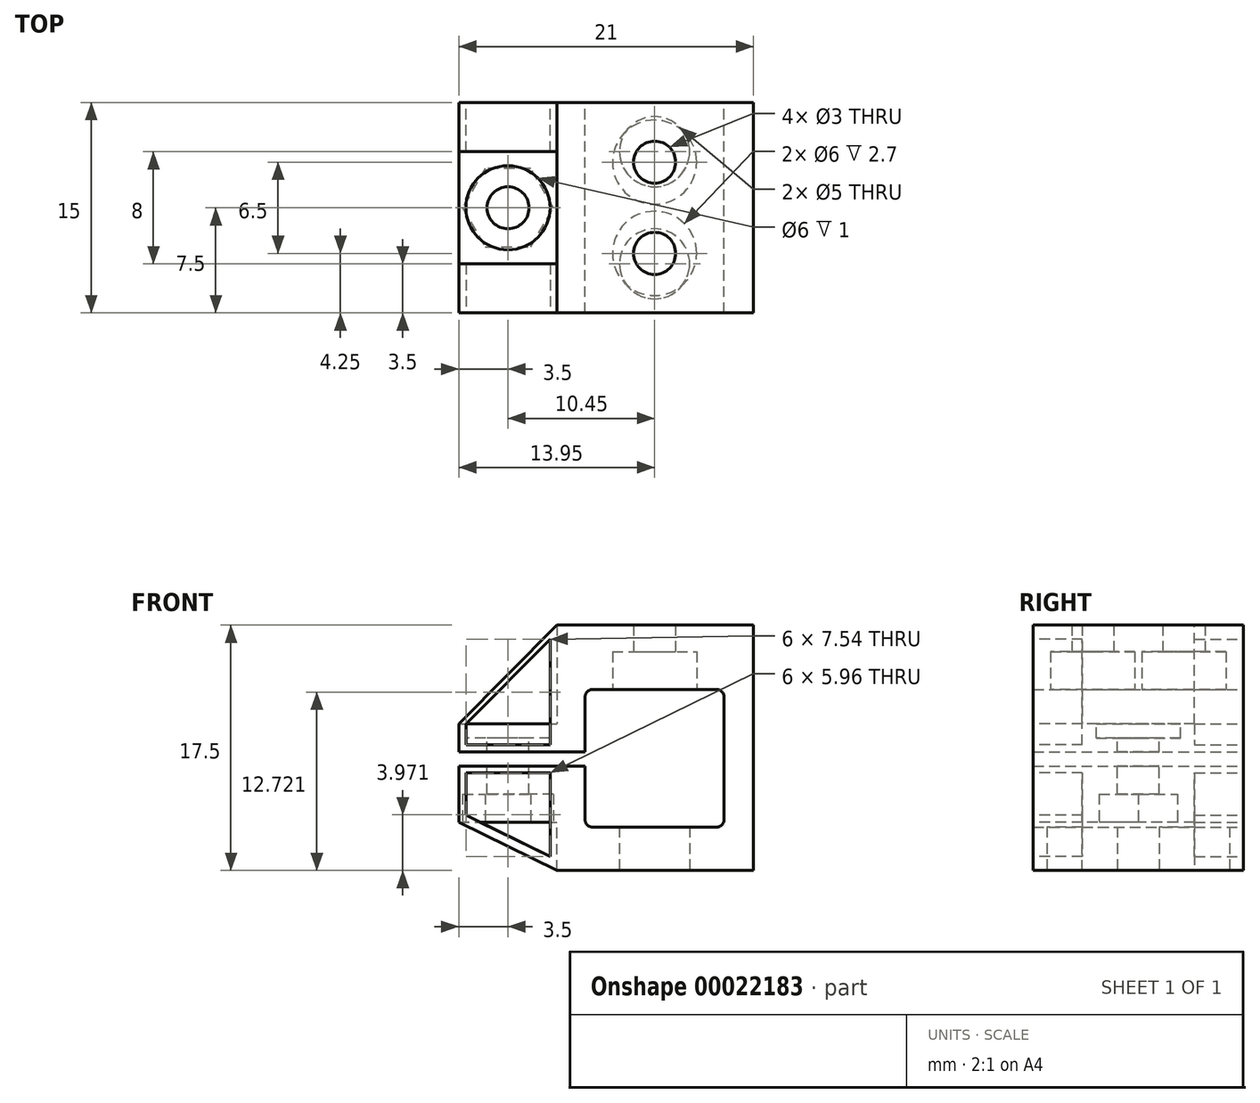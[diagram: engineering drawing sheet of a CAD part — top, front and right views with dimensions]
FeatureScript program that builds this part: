
annotation { "Feature Type Name" : "Feature", "Feature Type Description" : "" }
export const myFeature = defineFeature(function(context is Context, id is Id, definition is map)
    precondition{}
    {
        {
            var Q0;
            Q0=qCreatedBy(makeId("Front.planeOp"),FACE);
            var sketch = newSketch(context, id + "F0", { "sketchPlane" : qUnion([Q0])});
            skLineSegment(sketch, "E0.rect.bottom", {"start": v(-4.45, 4.9) * mm, "end": v(4.45, 4.9) * mm});
            skLineSegment(sketch, "E0.rect.top", {"start": v(-4.45, -4.9) * mm, "end": v(4.45, -4.9) * mm});
            skLineSegment(sketch, "E0.rect.left", {"start": v(-4.95, 4.4) * mm, "end": v(-4.95, -4.4) * mm});
            skLineSegment(sketch, "E0.rect.right", {"start": v(4.95, 4.4) * mm, "end": v(4.95, -4.4) * mm});
            skPoint(sketch, "E0.rect.middle", {"position": v(0, 0) * mm});
            skPoint(sketch, "E1.visualSharp", {"position": v(-4.95, 4.9) * mm});
            skArc(sketch, "E1.filletArc", {"start": v(-4.45, 4.9) * mm, "mid": v(-4.8, 4.75) * mm, "end": v(-4.95, 4.4) * mm});
            skPoint(sketch, "E2.visualSharp", {"position": v(4.95, 4.9) * mm});
            skArc(sketch, "E2.filletArc", {"start": v(4.95, 4.4) * mm, "mid": v(4.8, 4.75) * mm, "end": v(4.45, 4.9) * mm});
            skPoint(sketch, "E3.visualSharp", {"position": v(4.95, -4.9) * mm});
            skArc(sketch, "E3.filletArc", {"start": v(4.45, -4.9) * mm, "mid": v(4.8, -4.75) * mm, "end": v(4.95, -4.4) * mm});
            skPoint(sketch, "E4.visualSharp", {"position": v(-4.95, -4.9) * mm});
            skArc(sketch, "E4.filletArc", {"start": v(-4.95, -4.4) * mm, "mid": v(-4.8, -4.75) * mm, "end": v(-4.45, -4.9) * mm});
            skLineSegment(sketch, "E5", {"start": v(-4.95, -0.55) * mm, "end": v(-6.95, -0.55) * mm});
            skLineSegment(sketch, "E6", {"start": v(-6.95, -0.55) * mm, "end": v(-6.95, -8) * mm});
            skLineSegment(sketch, "E7", {"start": v(-6.95, -8) * mm, "end": v(7.05, -8) * mm});
            skLineSegment(sketch, "E8", {"start": v(7.05, -8) * mm, "end": v(7.05, 9.5) * mm});
            skLineSegment(sketch, "E9", {"start": v(7.05, 9.5) * mm, "end": v(-6.95, 9.5) * mm});
            skLineSegment(sketch, "E10", {"start": v(-6.95, 9.5) * mm, "end": v(-6.95, 0.45) * mm});
            skLineSegment(sketch, "E11", {"start": v(-6.95, 0.45) * mm, "end": v(-4.95, 0.45) * mm});
            skSolve(sketch);
        }
        {
            var Q0;
            Q0=makeQuery(id+"F0.imprint","IMPRINT",FACE,{"disambiguationData":[TD([[makeQuery(id+"F0.imprint","IMPRINT",EDGE,{"derivedFrom":sQuery(id+"F0.wireOp",EDGE,"E0.rect.bottom")}),1.0]])]});
            extrude(context, id + "F1", {"entities" : qUnion([Q0]), "depth" : 15 * mm});
        }
        {
            var Q0;
            Q0=makeQuery(id+"F1.opExtrude","SWEPT_FACE",FACE,{"disambiguationData":[OSD([sQuery(id+"F0.wireOp",EDGE,"E10")])]});
            var sketch = newSketch(context, id + "F2", { "sketchPlane" : qUnion([Q0])});
            skLineSegment(sketch, "E12.bottom", {"start": v(3.5, 0.45) * mm, "end": v(11.5, 0.45) * mm});
            skLineSegment(sketch, "E12.top", {"start": v(3.5, 2.45) * mm, "end": v(11.5, 2.45) * mm});
            skLineSegment(sketch, "E12.left", {"start": v(3.5, 0.45) * mm, "end": v(3.5, 2.45) * mm});
            skLineSegment(sketch, "E12.right", {"start": v(11.5, 0.45) * mm, "end": v(11.5, 2.45) * mm});
            skLineSegment(sketch, "E13.bottom", {"start": v(3.5, -0.55) * mm, "end": v(11.5, -0.55) * mm});
            skLineSegment(sketch, "E13.top", {"start": v(3.5, -4.55) * mm, "end": v(11.5, -4.55) * mm});
            skLineSegment(sketch, "E13.left", {"start": v(3.5, -0.55) * mm, "end": v(3.5, -4.55) * mm});
            skLineSegment(sketch, "E13.right", {"start": v(11.5, -0.55) * mm, "end": v(11.5, -4.55) * mm});
            skSolve(sketch);
        }
        {
            var Q0;
            Q0 = qSketchRegion(id + "F2", true);
            extrude(context, id + "F3", {"entities" : qUnion([Q0]), "operationType" : NewBodyOperationType.ADD, "depth" : 7 * mm});
        }
        {
            var Q0;
            Q0=makeQuery(id+"F3.opExtrude","SWEPT_FACE",FACE,{"disambiguationData":[OSD([sQuery(id+"F2.wireOp",EDGE,"E12.top")])]});
            var sketch = newSketch(context, id + "F4", { "sketchPlane" : qUnion([Q0])});
            skLineSegment(sketch, "E14", {"start": v(-10.45, -11.5) * mm, "end": v(-10.45, -3.5) * mm, "construction": true});
            skCircle(sketch, "E15", {"center": v(-10.45, -7.5) * mm, "radius": 1.5 * mm});
            skCircle(sketch, "E16", {"center": v(-10.45, -7.5) * mm, "radius": 3 * mm});
            skSolve(sketch);
        }
        {
            var Q0;
            Q0=makeQuery(id+"F4.imprint","IMPRINT",FACE,{"disambiguationData":[TD([[makeQuery(id+"F4.imprint","IMPRINT",EDGE,{"derivedFrom":sQuery(id+"F4.wireOp",EDGE,"E15")}),1.0]])]});
            extrude(context, id + "F5", {"entities" : qUnion([Q0]), "operationType" : NewBodyOperationType.REMOVE, "endBound" : BoundingType.THROUGH_ALL, "oppositeDirection" : true, "depth" : 25 * mm});
        }
        {
            var Q0;
            Q0 = qSketchRegion(id + "F4", true);
            extrude(context, id + "F6", {"entities" : qUnion([Q0]), "operationType" : NewBodyOperationType.REMOVE, "oppositeDirection" : true, "depth" : 1 * mm});
        }
        {
            var Q0;
            Q0=makeQuery(id+"F1.opExtrude","SWEPT_FACE",FACE,{"disambiguationData":[OSD([sQuery(id+"F0.wireOp",EDGE,"E0.rect.bottom")])]});
            var sketch = newSketch(context, id + "F7", { "sketchPlane" : qUnion([Q0])});
            skLineSegment(sketch, "E17", {"start": v(0, 15) * mm, "end": v(0, 0) * mm, "construction": true});
            skCircle(sketch, "E18", {"center": v(0, 10.75) * mm, "radius": 3 * mm});
            skCircle(sketch, "E19", {"center": v(0, 4.25) * mm, "radius": 3 * mm});
            skLineSegment(sketch, "E20", {"start": v(-4.45, 7.5) * mm, "end": v(4.45, 7.5) * mm, "construction": true});
            skCircle(sketch, "E21", {"center": v(0, 10.75) * mm, "radius": 1.5 * mm});
            skCircle(sketch, "E22", {"center": v(0, 4.25) * mm, "radius": 1.5 * mm});
            skSolve(sketch);
        }
        {
            var Q0;
            Q0=makeQuery(id+"F7.imprint","IMPRINT",FACE,{"disambiguationData":[TD([[makeQuery(id+"F7.imprint","IMPRINT",EDGE,{"derivedFrom":sQuery(id+"F7.wireOp",EDGE,"E21")}),1.0]])]});
            var Q1;
            Q1=makeQuery(id+"F7.imprint","IMPRINT",FACE,{"disambiguationData":[TD([[makeQuery(id+"F7.imprint","IMPRINT",EDGE,{"derivedFrom":sQuery(id+"F7.wireOp",EDGE,"E22")}),1.0]])]});
            extrude(context, id + "F8", {"entities" : qUnion([Q0, Q1]), "operationType" : NewBodyOperationType.REMOVE, "endBound" : BoundingType.THROUGH_ALL, "oppositeDirection" : true, "depth" : 25 * mm});
        }
        {
            var Q0;
            Q0 = qSketchRegion(id + "F7", true);
            extrude(context, id + "F9", {"entities" : qUnion([Q0]), "operationType" : NewBodyOperationType.REMOVE, "oppositeDirection" : true, "depth" : 2.7 * mm});
        }
        {
            var Q0;
            Q0=makeQuery(id+"F1.opExtrude","SWEPT_FACE",FACE,{"disambiguationData":[OSD([sQuery(id+"F0.wireOp",EDGE,"E7")])]});
            var sketch = newSketch(context, id + "F10", { "sketchPlane" : qUnion([Q0])});
            skLineSegment(sketch, "E23", {"start": v(0, 0) * mm, "end": v(0, 15) * mm, "construction": true});
            skPoint(sketch, "E24.rect.middle", {"position": v(0, 7.5) * mm});
            skCircle(sketch, "E25", {"center": v(0, 11.5) * mm, "radius": 2.5 * mm});
            skCircle(sketch, "E26", {"center": v(0, 3.5) * mm, "radius": 2.5 * mm});
            skSolve(sketch);
        }
        {
            var Q0;
            Q0 = qSketchRegion(id + "F10", true);
            var Q1;
            Q1=makeQuery(id+"F1.opExtrude","SWEPT_FACE",FACE,{"disambiguationData":[OSD([sQuery(id+"F0.wireOp",EDGE,"E0.rect.top")])]});
            extrude(context, id + "F11", {"entities" : qUnion([Q0]), "operationType" : NewBodyOperationType.REMOVE, "endBound" : BoundingType.UP_TO_SURFACE, "oppositeDirection" : true, "endBoundEntityFace" : qUnion([Q1]), "depth" : 25 * mm});
        }
        {
            var Q0;
            Q0=makeQuery(id+"F3.opExtrude","SWEPT_FACE",FACE,{"disambiguationData":[OSD([sQuery(id+"F2.wireOp",EDGE,"E13.top")])]});
            var sketch = newSketch(context, id + "F12", { "sketchPlane" : qUnion([Q0])});
            skCircle(sketch, "E27.cCircle", {"center": v(-10.45, 7.5) * mm, "radius": 2.8 * mm, "construction": true});
            skLineSegment(sketch, "E27.0", {"start": v(-8.83, 4.7) * mm, "end": v(-12.07, 4.7) * mm});
            skLineSegment(sketch, "E27.1", {"start": v(-12.07, 4.7) * mm, "end": v(-13.68, 7.5) * mm});
            skLineSegment(sketch, "E27.2", {"start": v(-13.68, 7.5) * mm, "end": v(-12.07, 10.3) * mm});
            skLineSegment(sketch, "E27.3", {"start": v(-12.07, 10.3) * mm, "end": v(-8.83, 10.3) * mm});
            skLineSegment(sketch, "E27.4", {"start": v(-8.83, 10.3) * mm, "end": v(-7.22, 7.5) * mm});
            skLineSegment(sketch, "E27.5", {"start": v(-7.22, 7.5) * mm, "end": v(-8.83, 4.7) * mm});
            skPoint(sketch, "E27.0.midPoint", {"position": v(-10.45, 4.7) * mm});
            skSolve(sketch);
        }
        {
            var Q0;
            Q0 = qSketchRegion(id + "F12", true);
            extrude(context, id + "F13", {"entities" : qUnion([Q0]), "operationType" : NewBodyOperationType.REMOVE, "oppositeDirection" : true, "depth" : 2 * mm});
        }
        {
            var Q0;
            Q0=makeQuery(id+"F1.opExtrude","CAP_FACE",FACE,{"disambiguationData":[OSD([sQuery(id+"F0.wireOp",EDGE,"E0.rect.bottom"),sQuery(id+"F0.wireOp",EDGE,"E0.rect.top"),sQuery(id+"F0.wireOp",EDGE,"E0.rect.left"),sQuery(id+"F0.wireOp",EDGE,"E0.rect.right"),sQuery(id+"F0.wireOp",EDGE,"E1.filletArc"),sQuery(id+"F0.wireOp",EDGE,"E2.filletArc"),sQuery(id+"F0.wireOp",EDGE,"E3.filletArc"),sQuery(id+"F0.wireOp",EDGE,"E4.filletArc"),sQuery(id+"F0.wireOp",EDGE,"E5"),sQuery(id+"F0.wireOp",EDGE,"E6"),sQuery(id+"F0.wireOp",EDGE,"E7"),sQuery(id+"F0.wireOp",EDGE,"E8"),sQuery(id+"F0.wireOp",EDGE,"E9"),sQuery(id+"F0.wireOp",EDGE,"E10"),sQuery(id+"F0.wireOp",EDGE,"E11")])],"isStart":true});
            var sketch = newSketch(context, id + "F14", { "sketchPlane" : qUnion([Q0])});
            skLineSegment(sketch, "E28", {"start": v(6.95, 9.5) * mm, "end": v(13.95, 2.45) * mm});
            skLineSegment(sketch, "E29", {"start": v(13.95, 2.45) * mm, "end": v(13.95, 0.45) * mm});
            skLineSegment(sketch, "E30", {"start": v(13.95, 0.45) * mm, "end": v(6.95, 0.45) * mm});
            skLineSegment(sketch, "E31", {"start": v(6.95, 0.45) * mm, "end": v(6.95, 9.5) * mm});
            skLineSegment(sketch, "E32", {"start": v(7.45, 8.5) * mm, "end": v(13.45, 2.45) * mm});
            skLineSegment(sketch, "E33", {"start": v(13.45, 2.45) * mm, "end": v(13.45, 0.95) * mm});
            skLineSegment(sketch, "E34", {"start": v(13.45, 0.95) * mm, "end": v(7.45, 0.95) * mm});
            skLineSegment(sketch, "E35", {"start": v(7.45, 0.95) * mm, "end": v(7.45, 8.5) * mm});
            skSolve(sketch);
        }
        {
            var Q0;
            Q0=makeQuery(id+"F14.imprint","IMPRINT",FACE,{"disambiguationData":[TD([[makeQuery(id+"F14.imprint","IMPRINT",EDGE,{"derivedFrom":sQuery(id+"F14.wireOp",EDGE,"E28")}),-1.0]])]});
            var Q1;
            Q1=makeQuery(id+"F3.opExtrude","SWEPT_FACE",FACE,{"disambiguationData":[OSD([sQuery(id+"F2.wireOp",EDGE,"E12.left")])]});
            extrude(context, id + "F15", {"entities" : qUnion([Q0]), "operationType" : NewBodyOperationType.ADD, "endBound" : BoundingType.UP_TO_SURFACE, "oppositeDirection" : true, "endBoundEntityFace" : qUnion([Q1]), "depth" : 25 * mm});
        }
        {
            var Q0;
            Q0=makeQuery(id+"F1.opExtrude","CAP_FACE",FACE,{"disambiguationData":[OSD([sQuery(id+"F0.wireOp",EDGE,"E0.rect.bottom"),sQuery(id+"F0.wireOp",EDGE,"E0.rect.top"),sQuery(id+"F0.wireOp",EDGE,"E0.rect.left"),sQuery(id+"F0.wireOp",EDGE,"E0.rect.right"),sQuery(id+"F0.wireOp",EDGE,"E1.filletArc"),sQuery(id+"F0.wireOp",EDGE,"E2.filletArc"),sQuery(id+"F0.wireOp",EDGE,"E3.filletArc"),sQuery(id+"F0.wireOp",EDGE,"E4.filletArc"),sQuery(id+"F0.wireOp",EDGE,"E5"),sQuery(id+"F0.wireOp",EDGE,"E6"),sQuery(id+"F0.wireOp",EDGE,"E7"),sQuery(id+"F0.wireOp",EDGE,"E8"),sQuery(id+"F0.wireOp",EDGE,"E9"),sQuery(id+"F0.wireOp",EDGE,"E10"),sQuery(id+"F0.wireOp",EDGE,"E11")])],"isStart":false});
            var sketch = newSketch(context, id + "F16", { "sketchPlane" : qUnion([Q0])});
            skLineSegment(sketch, "E36", {"start": v(-6.95, 9.5) * mm, "end": v(-6.95, 0.45) * mm});
            skLineSegment(sketch, "E37", {"start": v(-6.95, 0.45) * mm, "end": v(-13.95, 0.45) * mm});
            skLineSegment(sketch, "E38", {"start": v(-13.95, 0.45) * mm, "end": v(-13.95, 2.45) * mm});
            skLineSegment(sketch, "E39", {"start": v(-13.95, 2.45) * mm, "end": v(-6.95, 9.5) * mm});
            skLineSegment(sketch, "E40", {"start": v(-7.45, 8.5) * mm, "end": v(-13.45, 2.45) * mm});
            skLineSegment(sketch, "E41", {"start": v(-13.45, 2.45) * mm, "end": v(-13.45, 0.95) * mm});
            skLineSegment(sketch, "E42", {"start": v(-13.45, 0.95) * mm, "end": v(-7.45, 0.95) * mm});
            skLineSegment(sketch, "E43", {"start": v(-7.45, 0.95) * mm, "end": v(-7.45, 8.5) * mm});
            skSolve(sketch);
        }
        {
            var Q0;
            Q0=makeQuery(id+"F16.imprint","IMPRINT",FACE,{"disambiguationData":[TD([[makeQuery(id+"F16.imprint","IMPRINT",EDGE,{"derivedFrom":sQuery(id+"F16.wireOp",EDGE,"E36")}),-1.0]])]});
            var Q1;
            Q1=makeQuery(id+"F3.opExtrude","SWEPT_FACE",FACE,{"disambiguationData":[OSD([sQuery(id+"F2.wireOp",EDGE,"E12.right")])]});
            extrude(context, id + "F17", {"entities" : qUnion([Q0]), "operationType" : NewBodyOperationType.ADD, "endBound" : BoundingType.UP_TO_SURFACE, "oppositeDirection" : true, "endBoundEntityFace" : qUnion([Q1]), "depth" : 25 * mm});
        }
        {
            var Q0;
            Q0=makeQuery(id+"F15.boolean.opBoolean","MERGE",FACE,{"derivedFrom":[makeQuery(id+"F1.opExtrude","CAP_FACE",FACE,{"disambiguationData":[OSD([sQuery(id+"F0.wireOp",EDGE,"E0.rect.bottom"),sQuery(id+"F0.wireOp",EDGE,"E0.rect.top"),sQuery(id+"F0.wireOp",EDGE,"E0.rect.left"),sQuery(id+"F0.wireOp",EDGE,"E0.rect.right"),sQuery(id+"F0.wireOp",EDGE,"E1.filletArc"),sQuery(id+"F0.wireOp",EDGE,"E2.filletArc"),sQuery(id+"F0.wireOp",EDGE,"E3.filletArc"),sQuery(id+"F0.wireOp",EDGE,"E4.filletArc"),sQuery(id+"F0.wireOp",EDGE,"E5"),sQuery(id+"F0.wireOp",EDGE,"E6"),sQuery(id+"F0.wireOp",EDGE,"E7"),sQuery(id+"F0.wireOp",EDGE,"E8"),sQuery(id+"F0.wireOp",EDGE,"E9"),sQuery(id+"F0.wireOp",EDGE,"E10"),sQuery(id+"F0.wireOp",EDGE,"E11")])],"isStart":true}),makeQuery(id+"F15.opExtrude","CAP_FACE",FACE,{"disambiguationData":[OSD([sQuery(id+"F14.wireOp",EDGE,"E28"),sQuery(id+"F14.wireOp",EDGE,"E29"),sQuery(id+"F14.wireOp",EDGE,"E30"),sQuery(id+"F14.wireOp",EDGE,"E31"),sQuery(id+"F14.wireOp",EDGE,"E32"),sQuery(id+"F14.wireOp",EDGE,"E33"),sQuery(id+"F14.wireOp",EDGE,"E34"),sQuery(id+"F14.wireOp",EDGE,"E35")])],"isStart":true})]});
            var sketch = newSketch(context, id + "F18", { "sketchPlane" : qUnion([Q0])});
            skLineSegment(sketch, "E44", {"start": v(6.95, -8) * mm, "end": v(6.95, -0.55) * mm});
            skLineSegment(sketch, "E45", {"start": v(6.95, -0.55) * mm, "end": v(13.95, -0.55) * mm});
            skLineSegment(sketch, "E46", {"start": v(13.95, -0.55) * mm, "end": v(13.95, -4.55) * mm});
            skLineSegment(sketch, "E47", {"start": v(13.95, -4.55) * mm, "end": v(6.95, -8) * mm});
            skLineSegment(sketch, "E48", {"start": v(7.45, -7) * mm, "end": v(7.45, -1.05) * mm});
            skLineSegment(sketch, "E49", {"start": v(7.45, -1.05) * mm, "end": v(13.45, -1.05) * mm});
            skLineSegment(sketch, "E50", {"start": v(13.45, -1.05) * mm, "end": v(13.45, -4.05) * mm});
            skLineSegment(sketch, "E51", {"start": v(13.45, -4.05) * mm, "end": v(7.45, -7) * mm});
            skSolve(sketch);
        }
        {
            var Q0;
            Q0=makeQuery(id+"F18.imprint","IMPRINT",FACE,{"disambiguationData":[TD([[makeQuery(id+"F18.imprint","IMPRINT",EDGE,{"derivedFrom":sQuery(id+"F18.wireOp",EDGE,"E44")}),1.0]])]});
            var Q1;
            Q1=makeQuery(id+"F3.opExtrude","SWEPT_FACE",FACE,{"disambiguationData":[OSD([sQuery(id+"F2.wireOp",EDGE,"E13.left")])]});
            extrude(context, id + "F19", {"entities" : qUnion([Q0]), "operationType" : NewBodyOperationType.ADD, "endBound" : BoundingType.UP_TO_SURFACE, "oppositeDirection" : true, "endBoundEntityFace" : qUnion([Q1]), "depth" : 25 * mm});
        }
        {
            var Q0;
            Q0=makeQuery(id+"F17.boolean.opBoolean","MERGE",FACE,{"derivedFrom":[makeQuery(id+"F1.opExtrude","CAP_FACE",FACE,{"disambiguationData":[OSD([sQuery(id+"F0.wireOp",EDGE,"E0.rect.bottom"),sQuery(id+"F0.wireOp",EDGE,"E0.rect.top"),sQuery(id+"F0.wireOp",EDGE,"E0.rect.left"),sQuery(id+"F0.wireOp",EDGE,"E0.rect.right"),sQuery(id+"F0.wireOp",EDGE,"E1.filletArc"),sQuery(id+"F0.wireOp",EDGE,"E2.filletArc"),sQuery(id+"F0.wireOp",EDGE,"E3.filletArc"),sQuery(id+"F0.wireOp",EDGE,"E4.filletArc"),sQuery(id+"F0.wireOp",EDGE,"E5"),sQuery(id+"F0.wireOp",EDGE,"E6"),sQuery(id+"F0.wireOp",EDGE,"E7"),sQuery(id+"F0.wireOp",EDGE,"E8"),sQuery(id+"F0.wireOp",EDGE,"E9"),sQuery(id+"F0.wireOp",EDGE,"E10"),sQuery(id+"F0.wireOp",EDGE,"E11")])],"isStart":false}),makeQuery(id+"F17.opExtrude","CAP_FACE",FACE,{"disambiguationData":[OSD([sQuery(id+"F16.wireOp",EDGE,"E36"),sQuery(id+"F16.wireOp",EDGE,"E37"),sQuery(id+"F16.wireOp",EDGE,"E38"),sQuery(id+"F16.wireOp",EDGE,"E39"),sQuery(id+"F16.wireOp",EDGE,"E40"),sQuery(id+"F16.wireOp",EDGE,"E41"),sQuery(id+"F16.wireOp",EDGE,"E42"),sQuery(id+"F16.wireOp",EDGE,"E43")])],"isStart":true})]});
            var sketch = newSketch(context, id + "F20", { "sketchPlane" : qUnion([Q0])});
            skLineSegment(sketch, "E52", {"start": v(-6.95, -0.55) * mm, "end": v(-13.95, -0.55) * mm});
            skLineSegment(sketch, "E53", {"start": v(-13.95, -0.55) * mm, "end": v(-13.95, -4.55) * mm});
            skLineSegment(sketch, "E54", {"start": v(-13.95, -4.55) * mm, "end": v(-6.95, -8) * mm});
            skLineSegment(sketch, "E55", {"start": v(-7.45, -1.05) * mm, "end": v(-7.45, -7) * mm});
            skLineSegment(sketch, "E56", {"start": v(-7.45, -7) * mm, "end": v(-13.45, -4.05) * mm});
            skLineSegment(sketch, "E57", {"start": v(-13.45, -4.05) * mm, "end": v(-13.45, -1.05) * mm});
            skLineSegment(sketch, "E58", {"start": v(-13.45, -1.05) * mm, "end": v(-7.45, -1.05) * mm});
            skSolve(sketch);
        }
        {
            var Q0;
            Q0=makeQuery(id+"F20.imprint","IMPRINT",FACE,{"disambiguationData":[TD([[makeQuery(id+"F20.imprint","IMPRINT",EDGE,{"derivedFrom":sQuery(id+"F20.wireOp",EDGE,"E52")}),1.0]])]});
            var Q1;
            Q1=makeQuery(id+"F3.opExtrude","SWEPT_FACE",FACE,{"disambiguationData":[OSD([sQuery(id+"F2.wireOp",EDGE,"E13.right")])]});
            extrude(context, id + "F21", {"entities" : qUnion([Q0]), "operationType" : NewBodyOperationType.ADD, "endBound" : BoundingType.UP_TO_SURFACE, "oppositeDirection" : true, "endBoundEntityFace" : qUnion([Q1]), "depth" : 25 * mm});
        }
    });
